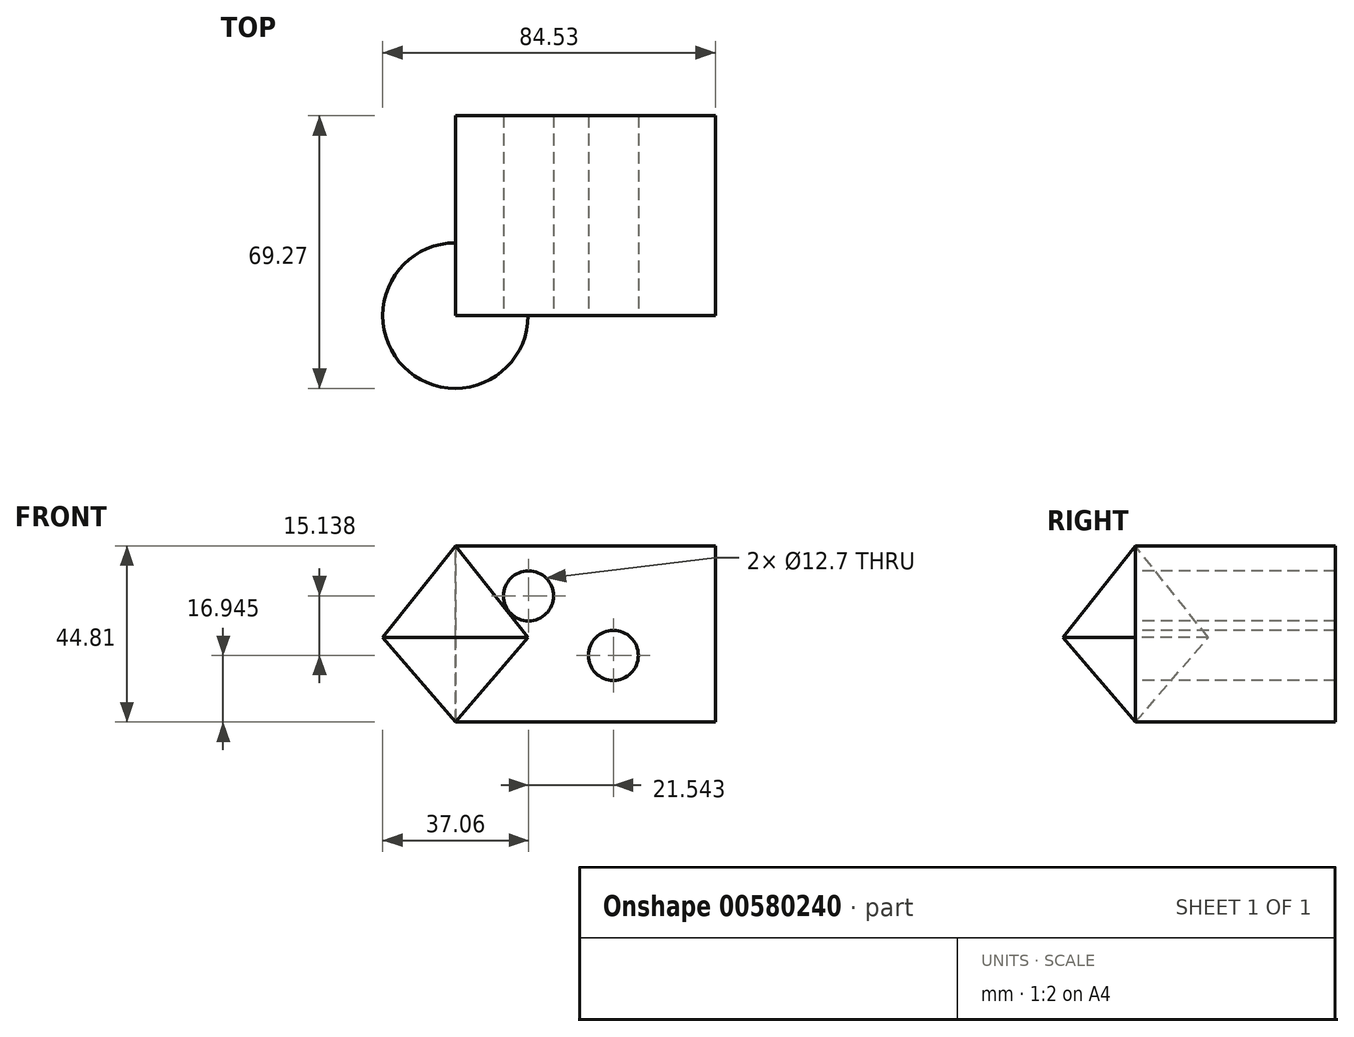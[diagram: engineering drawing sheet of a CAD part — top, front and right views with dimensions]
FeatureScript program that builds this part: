
annotation { "Feature Type Name" : "Feature", "Feature Type Description" : "" }
export const myFeature = defineFeature(function(context is Context, id is Id, definition is map)
    precondition{}
    {
        {
            var Q0;
            Q0=qCreatedBy(makeId("Front.planeOp"),FACE);
            var sketch = newSketch(context, id + "F0", { "sketchPlane" : qUnion([Q0])});
            skLineSegment(sketch, "E0.bottom", {"start": v(0, 44.81) * mm, "end": v(66.06, 44.81) * mm});
            skLineSegment(sketch, "E0.top", {"start": v(0, 0) * mm, "end": v(66.06, 0) * mm});
            skLineSegment(sketch, "E0.left", {"start": v(0, 44.81) * mm, "end": v(0, 0) * mm});
            skLineSegment(sketch, "E0.right", {"start": v(66.06, 44.81) * mm, "end": v(66.06, 0) * mm});
            skSolve(sketch);
        }
        {
            var Q0;
            Q0 = qSketchRegion(id + "F0", true);
            extrude(context, id + "F1", {"entities" : qUnion([Q0]), "depth" : 50.8 * mm, "offsetDistance" : 25.4 * mm});
        }
        {
            var Q0;
            Q0=makeQuery(id+"F1.opExtrude","CAP_FACE",FACE,{"disambiguationData":[OSD([sQuery(id+"F0.wireOp",EDGE,"E0.bottom"),sQuery(id+"F0.wireOp",EDGE,"E0.top"),sQuery(id+"F0.wireOp",EDGE,"E0.left"),sQuery(id+"F0.wireOp",EDGE,"E0.right")])],"isStart":false});
            var sketch = newSketch(context, id + "F2", { "sketchPlane" : qUnion([Q0])});
            skCircle(sketch, "E1", {"center": v(18.59, 32.08) * mm, "radius": 9.04 * mm});
            skSolve(sketch);
        }
        {
            var Q0;
            Q0=sQuery(id+"F2.wireOp",VERTEX,"E1.center");
            var Q1;
            Q1=makeQuery(id+"F1.opExtrude","SWEPT_BODY",BODY,{"disambiguationData":[OSD([sQuery(id+"F0.wireOp",EDGE,"E0.bottom"),sQuery(id+"F0.wireOp",EDGE,"E0.top"),sQuery(id+"F0.wireOp",EDGE,"E0.left"),sQuery(id+"F0.wireOp",EDGE,"E0.right")])]});
            hole(context, id + "F3", {"style" : HoleStyle.SIMPLE, "endStyle" : HoleEndStyle.THROUGH, "holeDiameter" : 12.7 * mm, "isTappedThrough" : true, "tappedDepth" : 12.7 * mm, "tapClearance" : 3, "locations" : qUnion([Q0]), "scope" : qUnion([Q1])});
        }
        {
            var Q0;
            Q0=qCreatedBy(makeId("Front.planeOp"),FACE);
            var sketch = newSketch(context, id + "F4", { "sketchPlane" : qUnion([Q0])});
            skLineSegment(sketch, "E2", {"start": v(0, 46.5) * mm, "end": v(10.57, 68.67) * mm});
            skLineSegment(sketch, "E3", {"start": v(10.57, 68.67) * mm, "end": v(23.06, 56.44) * mm});
            skLineSegment(sketch, "E4", {"start": v(23.06, 56.44) * mm, "end": v(33.91, 67.52) * mm});
            skLineSegment(sketch, "E5", {"start": v(33.91, 67.52) * mm, "end": v(47.27, 50.07) * mm});
            skLineSegment(sketch, "E6", {"start": v(47.27, 50.07) * mm, "end": v(61.03, 67.52) * mm});
            skLineSegment(sketch, "E7", {"start": v(61.03, 67.52) * mm, "end": v(66.12, 45.23) * mm});
            skLineSegment(sketch, "E8", {"start": v(66.12, 45.23) * mm, "end": v(0, 45.23) * mm});
            skSolve(sketch);
        }
        {
            var Q0;
            Q0=sQuery(id+"F4.wireOp",EDGE,"E2");
            var Q1;
            Q1=sQuery(id+"F4.wireOp",EDGE,"E3");
            var Q2;
            Q2=sQuery(id+"F4.wireOp",EDGE,"E4");
            var Q3;
            Q3=sQuery(id+"F4.wireOp",EDGE,"E5");
            var Q4;
            Q4=sQuery(id+"F4.wireOp",EDGE,"E6");
            var Q5;
            Q5=sQuery(id+"F4.wireOp",EDGE,"E7");
            var Q6;
            Q6=sQuery(id+"F4.wireOp",EDGE,"E8");
            extrude(context, id + "F5", {"bodyType" : ToolBodyType.SURFACE, "surfaceEntities" : qUnion([Q0, Q1, Q2, Q3, Q4, Q5, Q6]), "depth" : 50.8 * mm, "offsetDistance" : 25.4 * mm});
        }
        {
            var Q0;
            Q0=makeQuery(id+"F1.opExtrude","CAP_FACE",FACE,{"disambiguationData":[OSD([sQuery(id+"F0.wireOp",EDGE,"E0.bottom"),sQuery(id+"F0.wireOp",EDGE,"E0.top"),sQuery(id+"F0.wireOp",EDGE,"E0.left"),sQuery(id+"F0.wireOp",EDGE,"E0.right")])],"isStart":false});
            var sketch = newSketch(context, id + "F6", { "sketchPlane" : qUnion([Q0])});
            skCircle(sketch, "E9", {"center": v(40.13, 16.94) * mm, "radius": 6.06 * mm});
            skSolve(sketch);
        }
        {
            var Q0;
            Q0=makeQuery(id+"F6.imprint","IMPRINT",FACE,{"disambiguationData":[TD([[makeQuery(id+"F6.imprint","IMPRINT",EDGE,{"derivedFrom":sQuery(id+"F6.wireOp",EDGE,"E9")}),-1.0]])]});
            var sketch = newSketch(context, id + "F7", { "sketchPlane" : qUnion([Q0])});
            skLineSegment(sketch, "E10", {"start": v(0, 44.72) * mm, "end": v(-18.47, 21.53) * mm});
            skLineSegment(sketch, "E11", {"start": v(-18.47, 21.53) * mm, "end": v(0, 0) * mm});
            skSolve(sketch);
        }
        {
            var Q0;
            {var subQ0=sQuery(id+"F7.wireOp",EDGE,"E10");Q0=makeQuery(id+"F7.imprint","IMPRINT",FACE,{"disambiguationData":[TD([[makeQuery(id+"F7.imprint","IMPRINT",EDGE,{"derivedFrom":subQ0}),1.0]])]});}
            var Q1;
            Q1=makeQuery(id+"F1.opExtrude","CAP_EDGE",EDGE,{"disambiguationData":[OSD([sQuery(id+"F0.wireOp",EDGE,"E0.left")])],"isStart":false});
            revolve(context, id + "F8", {"operationType" : NewBodyOperationType.ADD, "entities" : qUnion([Q0]), "axis" : qUnion([Q1]), "revolveType" : RevolveType.FULL});
        }
        {
            var Q0;
            Q0=sQuery(id+"F6.wireOp",VERTEX,"E9.center");
            var Q1;
            Q1=makeQuery(id+"F1.opExtrude","SWEPT_BODY",BODY,{"disambiguationData":[OSD([sQuery(id+"F0.wireOp",EDGE,"E0.bottom"),sQuery(id+"F0.wireOp",EDGE,"E0.top"),sQuery(id+"F0.wireOp",EDGE,"E0.left"),sQuery(id+"F0.wireOp",EDGE,"E0.right")])]});
            hole(context, id + "F9", {"style" : HoleStyle.SIMPLE, "endStyle" : HoleEndStyle.THROUGH, "holeDiameter" : 12.7 * mm, "majorDiameter" : 6.35 * mm, "isTappedThrough" : true, "tappedDepth" : 12.7 * mm, "tapClearance" : 3, "locations" : qUnion([Q0]), "scope" : qUnion([Q1])});
        }
    });
